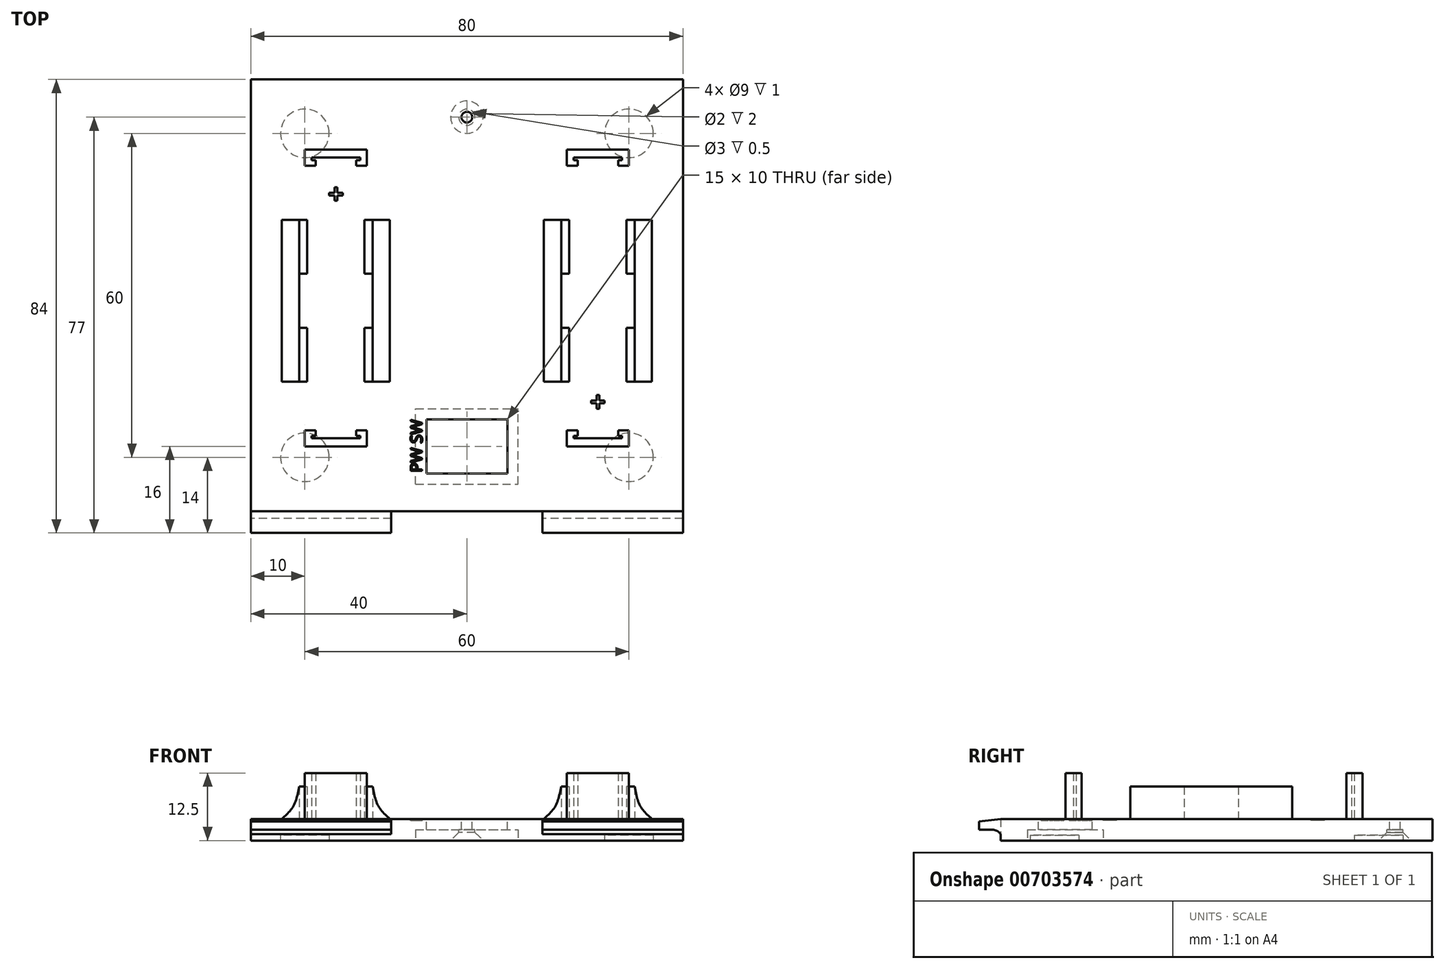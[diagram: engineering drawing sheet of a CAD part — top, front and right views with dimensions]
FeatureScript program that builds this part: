
annotation { "Feature Type Name" : "Feature", "Feature Type Description" : "" }
export const myFeature = defineFeature(function(context is Context, id is Id, definition is map)
    precondition{}
    {
        {
            var Q0;
            Q0=qCreatedBy(makeId("Top.planeOp"),FACE);
            var sketch = newSketch(context, id + "F0", { "sketchPlane" : qUnion([Q0])});
            skLineSegment(sketch, "E0.bottom", {"start": v(-40, 40) * mm, "end": v(40, 40) * mm});
            skLineSegment(sketch, "E0.top", {"start": v(-40, -40) * mm, "end": v(40, -40) * mm});
            skLineSegment(sketch, "E0.left", {"start": v(-40, 40) * mm, "end": v(-40, -40) * mm});
            skLineSegment(sketch, "E0.right", {"start": v(40, 40) * mm, "end": v(40, -40) * mm});
            skLineSegment(sketch, "E1.bottom", {"start": v(-40, -40) * mm, "end": v(-20, -40) * mm});
            skLineSegment(sketch, "E1.top", {"start": v(-40, -44) * mm, "end": v(-20, -44) * mm});
            skLineSegment(sketch, "E1.left", {"start": v(-40, -40) * mm, "end": v(-40, -44) * mm});
            skLineSegment(sketch, "E1.right", {"start": v(-20, -40) * mm, "end": v(-20, -44) * mm});
            skLineSegment(sketch, "E2.bottom", {"start": v(20, -40) * mm, "end": v(40, -40) * mm});
            skLineSegment(sketch, "E2.top", {"start": v(20, -44) * mm, "end": v(40, -44) * mm});
            skLineSegment(sketch, "E2.left", {"start": v(20, -40) * mm, "end": v(20, -44) * mm});
            skLineSegment(sketch, "E2.right", {"start": v(40, -40) * mm, "end": v(40, -44) * mm});
            skLineSegment(sketch, "E3", {"start": v(-20, -44) * mm, "end": v(20, -44) * mm});
            skLineSegment(sketch, "E4", {"start": v(-20, -40) * mm, "end": v(20, -40) * mm});
            skLineSegment(sketch, "E5", {"start": v(-14, -44) * mm, "end": v(-14, -40) * mm});
            skLineSegment(sketch, "E6", {"start": v(14, -44) * mm, "end": v(14, -40) * mm});
            skPoint(sketch, "E6.endSnap0", {"position": v(0, -40) * mm});
            skSolve(sketch);
        }
        {
            var Q0;
            Q0=makeQuery(id+"F0.imprint","IMPRINT",FACE,{"disambiguationData":[TD([[makeQuery(id+"F0.imprint","IMPRINT",EDGE,{"derivedFrom":sQuery(id+"F0.wireOp",EDGE,"E0.bottom")}),-1.0]])]});
            extrude(context, id + "F1", {"entities" : qUnion([Q0]), "depth" : 4 * mm, "offsetDistance" : 25 * mm});
        }
        {
            var Q0;
            Q0=makeQuery(id+"F1.opExtrude","CAP_FACE",FACE,{"disambiguationData":[OSD([sQuery(id+"F0.wireOp",EDGE,"E0.bottom"),sQuery(id+"F0.wireOp",EDGE,"E0.top"),sQuery(id+"F0.wireOp",EDGE,"E0.left"),sQuery(id+"F0.wireOp",EDGE,"E0.right")])],"isStart":false});
            var sketch = newSketch(context, id + "F2", { "sketchPlane" : qUnion([Q0])});
            skLineSegment(sketch, "E7.bottom", {"start": v(-30, 27) * mm, "end": v(-28, 27) * mm});
            skLineSegment(sketch, "E7.top", {"start": v(-30, 24) * mm, "end": v(-28, 24) * mm});
            skLineSegment(sketch, "E7.left", {"start": v(-30, 27) * mm, "end": v(-30, 24) * mm});
            skLineSegment(sketch, "E7.right", {"start": v(-28, 27) * mm, "end": v(-28, 24) * mm});
            skLineSegment(sketch, "E8.bottom", {"start": v(-20.5, 27) * mm, "end": v(-18.5, 27) * mm});
            skLineSegment(sketch, "E8.top", {"start": v(-20.5, 24) * mm, "end": v(-18.5, 24) * mm});
            skLineSegment(sketch, "E8.left", {"start": v(-20.5, 27) * mm, "end": v(-20.5, 24) * mm});
            skLineSegment(sketch, "E8.right", {"start": v(-18.5, 27) * mm, "end": v(-18.5, 24) * mm});
            skLineSegment(sketch, "E9", {"start": v(-28, 27) * mm, "end": v(-20.5, 27) * mm});
            skLineSegment(sketch, "E10", {"start": v(-28, 25) * mm, "end": v(-20.5, 25) * mm, "construction": true});
            skLineSegment(sketch, "E11", {"start": v(-28, 25.5) * mm, "end": v(-20.5, 25.5) * mm});
            skLineSegment(sketch, "E12", {"start": v(-28, 25.5) * mm, "end": v(-28.75, 25.5) * mm});
            skLineSegment(sketch, "E13", {"start": v(-28.75, 25.5) * mm, "end": v(-28.75, 25) * mm});
            skLineSegment(sketch, "E14", {"start": v(-28.75, 25) * mm, "end": v(-28, 25) * mm});
            skLineSegment(sketch, "E15", {"start": v(-20.5, 25.5) * mm, "end": v(-19.75, 25.5) * mm});
            skLineSegment(sketch, "E16", {"start": v(-19.75, 25.5) * mm, "end": v(-19.75, 25) * mm});
            skLineSegment(sketch, "E17", {"start": v(-19.75, 25) * mm, "end": v(-20.5, 25) * mm});
            skLineSegment(sketch, "E18.bottom", {"start": v(-18.5, -28) * mm, "end": v(-20.5, -28) * mm});
            skLineSegment(sketch, "E18.top", {"start": v(-18.5, -25) * mm, "end": v(-20.5, -25) * mm});
            skLineSegment(sketch, "E18.left", {"start": v(-18.5, -28) * mm, "end": v(-18.5, -25) * mm});
            skLineSegment(sketch, "E18.right", {"start": v(-20.5, -28) * mm, "end": v(-20.5, -25) * mm});
            skLineSegment(sketch, "E19.bottom", {"start": v(-28, -28) * mm, "end": v(-30, -28) * mm});
            skLineSegment(sketch, "E19.top", {"start": v(-28, -25) * mm, "end": v(-30, -25) * mm});
            skLineSegment(sketch, "E19.left", {"start": v(-28, -28) * mm, "end": v(-28, -25) * mm});
            skLineSegment(sketch, "E19.right", {"start": v(-30, -28) * mm, "end": v(-30, -25) * mm});
            skLineSegment(sketch, "E20", {"start": v(-20.5, -28) * mm, "end": v(-28, -28) * mm});
            skLineSegment(sketch, "E21", {"start": v(-20.5, -26) * mm, "end": v(-28, -26) * mm, "construction": true});
            skLineSegment(sketch, "E22", {"start": v(-20.5, -26.5) * mm, "end": v(-28, -26.5) * mm});
            skLineSegment(sketch, "E23", {"start": v(-20.5, -26.5) * mm, "end": v(-19.75, -26.5) * mm});
            skLineSegment(sketch, "E24", {"start": v(-19.75, -26.5) * mm, "end": v(-19.75, -26) * mm});
            skLineSegment(sketch, "E25", {"start": v(-19.75, -26) * mm, "end": v(-20.5, -26) * mm});
            skLineSegment(sketch, "E26", {"start": v(-28, -26.5) * mm, "end": v(-28.75, -26.5) * mm});
            skLineSegment(sketch, "E27", {"start": v(-28.75, -26.5) * mm, "end": v(-28.75, -26) * mm});
            skLineSegment(sketch, "E28", {"start": v(-28.75, -26) * mm, "end": v(-28, -26) * mm});
            skLineSegment(sketch, "E29.bottom", {"start": v(18.5, 27) * mm, "end": v(20.5, 27) * mm});
            skLineSegment(sketch, "E29.top", {"start": v(18.5, 24) * mm, "end": v(20.5, 24) * mm});
            skLineSegment(sketch, "E29.left", {"start": v(18.5, 27) * mm, "end": v(18.5, 24) * mm});
            skLineSegment(sketch, "E29.right", {"start": v(20.5, 27) * mm, "end": v(20.5, 24) * mm});
            skLineSegment(sketch, "E30.bottom", {"start": v(28, 27) * mm, "end": v(30, 27) * mm});
            skLineSegment(sketch, "E30.top", {"start": v(28, 24) * mm, "end": v(30, 24) * mm});
            skLineSegment(sketch, "E30.left", {"start": v(28, 27) * mm, "end": v(28, 24) * mm});
            skLineSegment(sketch, "E30.right", {"start": v(30, 27) * mm, "end": v(30, 24) * mm});
            skLineSegment(sketch, "E31", {"start": v(20.5, 27) * mm, "end": v(28, 27) * mm});
            skLineSegment(sketch, "E32", {"start": v(20.5, 25) * mm, "end": v(28, 25) * mm, "construction": true});
            skLineSegment(sketch, "E33", {"start": v(20.5, 25.5) * mm, "end": v(28, 25.5) * mm});
            skLineSegment(sketch, "E34", {"start": v(20.5, 25.5) * mm, "end": v(19.75, 25.5) * mm});
            skLineSegment(sketch, "E35", {"start": v(19.75, 25.5) * mm, "end": v(19.75, 25) * mm});
            skLineSegment(sketch, "E36", {"start": v(19.75, 25) * mm, "end": v(20.5, 25) * mm});
            skLineSegment(sketch, "E37", {"start": v(28, 25.5) * mm, "end": v(28.75, 25.5) * mm});
            skLineSegment(sketch, "E38", {"start": v(28.75, 25.5) * mm, "end": v(28.75, 25) * mm});
            skLineSegment(sketch, "E39", {"start": v(28.75, 25) * mm, "end": v(28, 25) * mm});
            skLineSegment(sketch, "E40.bottom", {"start": v(30, -28) * mm, "end": v(28, -28) * mm});
            skLineSegment(sketch, "E40.top", {"start": v(30, -25) * mm, "end": v(28, -25) * mm});
            skLineSegment(sketch, "E40.left", {"start": v(30, -28) * mm, "end": v(30, -25) * mm});
            skLineSegment(sketch, "E40.right", {"start": v(28, -28) * mm, "end": v(28, -25) * mm});
            skLineSegment(sketch, "E41.bottom", {"start": v(20.5, -28) * mm, "end": v(18.5, -28) * mm});
            skLineSegment(sketch, "E41.top", {"start": v(20.5, -25) * mm, "end": v(18.5, -25) * mm});
            skLineSegment(sketch, "E41.left", {"start": v(20.5, -28) * mm, "end": v(20.5, -25) * mm});
            skLineSegment(sketch, "E41.right", {"start": v(18.5, -28) * mm, "end": v(18.5, -25) * mm});
            skLineSegment(sketch, "E42", {"start": v(28, -28) * mm, "end": v(20.5, -28) * mm});
            skLineSegment(sketch, "E43", {"start": v(28, -26) * mm, "end": v(20.5, -26) * mm, "construction": true});
            skLineSegment(sketch, "E44", {"start": v(28, -26.5) * mm, "end": v(20.5, -26.5) * mm});
            skLineSegment(sketch, "E45", {"start": v(28, -26.5) * mm, "end": v(28.75, -26.5) * mm});
            skLineSegment(sketch, "E46", {"start": v(28.75, -26.5) * mm, "end": v(28.75, -26) * mm});
            skLineSegment(sketch, "E47", {"start": v(28.75, -26) * mm, "end": v(28, -26) * mm});
            skLineSegment(sketch, "E48", {"start": v(20.5, -26.5) * mm, "end": v(19.75, -26.5) * mm});
            skLineSegment(sketch, "E49", {"start": v(19.75, -26.5) * mm, "end": v(19.75, -26) * mm});
            skLineSegment(sketch, "E50", {"start": v(19.75, -26) * mm, "end": v(20.5, -26) * mm});
            skLineSegment(sketch, "E51", {"start": v(-18.5, 27) * mm, "end": v(18.5, 27) * mm, "construction": true});
            skLineSegment(sketch, "E52", {"start": v(-24.25, 25) * mm, "end": v(-24.25, -26) * mm, "construction": true});
            skLineSegment(sketch, "E53", {"start": v(24.25, 25) * mm, "end": v(24.25, -26) * mm, "construction": true});
            skLineSegment(sketch, "E54.bottom", {"start": v(-31.05, 14) * mm, "end": v(-29.55, 14) * mm});
            skLineSegment(sketch, "E54.top", {"start": v(-31.05, 4) * mm, "end": v(-29.55, 4) * mm});
            skLineSegment(sketch, "E54.left", {"start": v(-31.05, 14) * mm, "end": v(-31.05, 4) * mm});
            skLineSegment(sketch, "E54.right", {"start": v(-29.55, 14) * mm, "end": v(-29.55, 4) * mm});
            skLineSegment(sketch, "E55", {"start": v(-30, 24) * mm, "end": v(-42.81, 24) * mm, "construction": true});
            skLineSegment(sketch, "E56.bottom", {"start": v(-31.05, -6) * mm, "end": v(-29.55, -6) * mm});
            skLineSegment(sketch, "E56.top", {"start": v(-31.05, -16) * mm, "end": v(-29.55, -16) * mm});
            skLineSegment(sketch, "E56.left", {"start": v(-31.05, -6) * mm, "end": v(-31.05, -16) * mm});
            skLineSegment(sketch, "E56.right", {"start": v(-29.55, -6) * mm, "end": v(-29.55, -16) * mm});
            skLineSegment(sketch, "E57.MirrorCS", {"start": v(-18.95, 14) * mm, "end": v(-18.95, 4) * mm});
            skLineSegment(sketch, "E58.MirrorCS", {"start": v(-17.45, 14) * mm, "end": v(-17.45, 4) * mm});
            skLineSegment(sketch, "E59.MirrorCS", {"start": v(-17.45, 14) * mm, "end": v(-18.95, 14) * mm});
            skLineSegment(sketch, "E60.MirrorCS", {"start": v(-17.45, 4) * mm, "end": v(-18.95, 4) * mm});
            skLineSegment(sketch, "E61.MirrorCS", {"start": v(-18.95, -6) * mm, "end": v(-18.95, -16) * mm});
            skLineSegment(sketch, "E62.MirrorCS", {"start": v(-17.45, -6) * mm, "end": v(-17.45, -16) * mm});
            skLineSegment(sketch, "E63.MirrorCS", {"start": v(-17.45, -6) * mm, "end": v(-18.95, -6) * mm});
            skLineSegment(sketch, "E64.MirrorCS", {"start": v(-17.45, -16) * mm, "end": v(-18.95, -16) * mm});
            skLineSegment(sketch, "E65", {"start": v(18.5, 24) * mm, "end": v(3.37, 24) * mm, "construction": true});
            skLineSegment(sketch, "E66.bottom", {"start": v(17.45, 14) * mm, "end": v(18.95, 14) * mm});
            skLineSegment(sketch, "E66.top", {"start": v(17.45, 4) * mm, "end": v(18.95, 4) * mm});
            skLineSegment(sketch, "E66.left", {"start": v(17.45, 14) * mm, "end": v(17.45, 4) * mm});
            skLineSegment(sketch, "E66.right", {"start": v(18.95, 14) * mm, "end": v(18.95, 4) * mm});
            skLineSegment(sketch, "E67.bottom", {"start": v(17.45, -6) * mm, "end": v(18.95, -6) * mm});
            skLineSegment(sketch, "E67.top", {"start": v(17.45, -16) * mm, "end": v(18.95, -16) * mm});
            skLineSegment(sketch, "E67.left", {"start": v(17.45, -6) * mm, "end": v(17.45, -16) * mm});
            skLineSegment(sketch, "E67.right", {"start": v(18.95, -6) * mm, "end": v(18.95, -16) * mm});
            skLineSegment(sketch, "E68.MirrorCS", {"start": v(29.55, 14) * mm, "end": v(29.55, 4) * mm});
            skLineSegment(sketch, "E69.MirrorCS", {"start": v(31.05, 14) * mm, "end": v(31.05, 4) * mm});
            skLineSegment(sketch, "E70.MirrorCS", {"start": v(31.05, 4) * mm, "end": v(29.55, 4) * mm});
            skLineSegment(sketch, "E71.MirrorCS", {"start": v(31.05, 14) * mm, "end": v(29.55, 14) * mm});
            skLineSegment(sketch, "E72.MirrorCS", {"start": v(31.05, -6) * mm, "end": v(29.55, -6) * mm});
            skLineSegment(sketch, "E73.MirrorCS", {"start": v(29.55, -6) * mm, "end": v(29.55, -16) * mm});
            skLineSegment(sketch, "E74.MirrorCS", {"start": v(31.05, -6) * mm, "end": v(31.05, -16) * mm});
            skLineSegment(sketch, "E75.MirrorCS", {"start": v(31.05, -16) * mm, "end": v(29.55, -16) * mm});
            skLineSegment(sketch, "E76", {"start": v(-28, -25) * mm, "end": v(-20.5, -25) * mm, "construction": true});
            skLineSegment(sketch, "E77", {"start": v(20.5, -25) * mm, "end": v(28, -25) * mm, "construction": true});
            skLineSegment(sketch, "E78", {"start": v(20.5, 24) * mm, "end": v(28, 24) * mm, "construction": true});
            skLineSegment(sketch, "E79", {"start": v(-28, 24) * mm, "end": v(-20.5, 24) * mm, "construction": true});
            skLineSegment(sketch, "E80.bottom", {"start": v(-24.5, 20) * mm, "end": v(-24, 20) * mm});
            skLineSegment(sketch, "E80.top", {"start": v(-24.5, 17.5) * mm, "end": v(-24, 17.5) * mm});
            skLineSegment(sketch, "E80.left", {"start": v(-24.5, 20) * mm, "end": v(-24.5, 19) * mm});
            skLineSegment(sketch, "E80.right", {"start": v(-24, 20) * mm, "end": v(-24, 19) * mm});
            skLineSegment(sketch, "E81.bottom", {"start": v(-23, 19) * mm, "end": v(-24, 19) * mm});
            skLineSegment(sketch, "E81.top", {"start": v(-23, 18.5) * mm, "end": v(-24, 18.5) * mm});
            skLineSegment(sketch, "E81.left", {"start": v(-23, 19) * mm, "end": v(-23, 18.5) * mm});
            skLineSegment(sketch, "E81.right", {"start": v(-25.5, 19) * mm, "end": v(-25.5, 18.5) * mm});
            skLineSegment(sketch, "E82", {"start": v(-25.5, 18.75) * mm, "end": v(-23, 18.75) * mm, "construction": true});
            skLineSegment(sketch, "E83", {"start": v(-24.25, 20) * mm, "end": v(-24.25, 17.5) * mm, "construction": true});
            skLineSegment(sketch, "E84.trimOffspring", {"start": v(-24.5, 18.5) * mm, "end": v(-24.5, 17.5) * mm});
            skLineSegment(sketch, "E85.trimOffspring", {"start": v(-24.5, 18.5) * mm, "end": v(-25.5, 18.5) * mm});
            skLineSegment(sketch, "E86.trimOffspring", {"start": v(-24, 18.5) * mm, "end": v(-24, 17.5) * mm});
            skLineSegment(sketch, "E87.trimOffspring", {"start": v(-24.5, 19) * mm, "end": v(-25.5, 19) * mm});
            skLineSegment(sketch, "E88.bottom", {"start": v(24, -18.5) * mm, "end": v(24.5, -18.5) * mm});
            skLineSegment(sketch, "E88.top", {"start": v(24, -21) * mm, "end": v(24.5, -21) * mm});
            skLineSegment(sketch, "E88.left", {"start": v(24, -18.5) * mm, "end": v(24, -19.5) * mm});
            skLineSegment(sketch, "E88.right", {"start": v(24.5, -18.5) * mm, "end": v(24.5, -19.5) * mm});
            skLineSegment(sketch, "E89.bottom", {"start": v(25.5, -19.5) * mm, "end": v(24.5, -19.5) * mm});
            skLineSegment(sketch, "E89.top", {"start": v(25.5, -20) * mm, "end": v(24.5, -20) * mm});
            skLineSegment(sketch, "E89.left", {"start": v(25.5, -19.5) * mm, "end": v(25.5, -20) * mm});
            skLineSegment(sketch, "E89.right", {"start": v(23, -19.5) * mm, "end": v(23, -20) * mm});
            skLineSegment(sketch, "E90", {"start": v(23, -19.75) * mm, "end": v(25.5, -19.75) * mm, "construction": true});
            skLineSegment(sketch, "E91", {"start": v(24.25, -18.5) * mm, "end": v(24.25, -21) * mm, "construction": true});
            skLineSegment(sketch, "E92.trimOffspring", {"start": v(24, -20) * mm, "end": v(24, -21) * mm});
            skLineSegment(sketch, "E93.trimOffspring", {"start": v(24, -20) * mm, "end": v(23, -20) * mm});
            skLineSegment(sketch, "E94.trimOffspring", {"start": v(24.5, -20) * mm, "end": v(24.5, -21) * mm});
            skLineSegment(sketch, "E95.trimOffspring", {"start": v(24, -19.5) * mm, "end": v(23, -19.5) * mm});
            skSolve(sketch);
        }
        {
            var Q0;
            Q0=makeQuery(id+"F2.imprint","IMPRINT",FACE,{"disambiguationData":[TD([[makeQuery(id+"F2.imprint","IMPRINT",EDGE,{"derivedFrom":sQuery(id+"F2.wireOp",EDGE,"E56.bottom")}),-1.0]])]});
            var Q1;
            Q1=makeQuery(id+"F2.imprint","IMPRINT",FACE,{"disambiguationData":[TD([[makeQuery(id+"F2.imprint","IMPRINT",EDGE,{"derivedFrom":sQuery(id+"F2.wireOp",EDGE,"E61.MirrorCS")}),1.0]])]});
            var Q2;
            Q2=makeQuery(id+"F2.imprint","IMPRINT",FACE,{"disambiguationData":[TD([[makeQuery(id+"F2.imprint","IMPRINT",EDGE,{"derivedFrom":sQuery(id+"F2.wireOp",EDGE,"E57.MirrorCS")}),1.0]])]});
            var Q3;
            Q3=makeQuery(id+"F2.imprint","IMPRINT",FACE,{"disambiguationData":[TD([[makeQuery(id+"F2.imprint","IMPRINT",EDGE,{"derivedFrom":sQuery(id+"F2.wireOp",EDGE,"E54.bottom")}),-1.0]])]});
            var Q4;
            Q4=makeQuery(id+"F2.imprint","IMPRINT",FACE,{"disambiguationData":[TD([[makeQuery(id+"F2.imprint","IMPRINT",EDGE,{"derivedFrom":sQuery(id+"F2.wireOp",EDGE,"E67.bottom")}),-1.0]])]});
            var Q5;
            Q5=makeQuery(id+"F2.imprint","IMPRINT",FACE,{"disambiguationData":[TD([[makeQuery(id+"F2.imprint","IMPRINT",EDGE,{"derivedFrom":sQuery(id+"F2.wireOp",EDGE,"E66.bottom")}),-1.0]])]});
            var Q6;
            Q6=makeQuery(id+"F2.imprint","IMPRINT",FACE,{"disambiguationData":[TD([[makeQuery(id+"F2.imprint","IMPRINT",EDGE,{"derivedFrom":sQuery(id+"F2.wireOp",EDGE,"E68.MirrorCS")}),1.0]])]});
            var Q7;
            Q7=makeQuery(id+"F2.imprint","IMPRINT",FACE,{"disambiguationData":[TD([[makeQuery(id+"F2.imprint","IMPRINT",EDGE,{"derivedFrom":sQuery(id+"F2.wireOp",EDGE,"E72.MirrorCS")}),1.0]])]});
            extrude(context, id + "F3", {"entities" : qUnion([Q0, Q1, Q2, Q3, Q4, Q5, Q6, Q7]), "operationType" : NewBodyOperationType.ADD, "depth" : 6 * mm, "offsetDistance" : 25 * mm});
        }
        {
            var Q0;
            {var subQ1=sQuery(id+"F2.wireOp",EDGE,"E7.bottom");Q0=makeQuery(id+"F2.imprint","IMPRINT",FACE,{"disambiguationData":[TD([[makeQuery(id+"F2.imprint","IMPRINT",EDGE,{"derivedFrom":subQ1}),-1.0]])]});}
            var Q1;
            {var subQ0=sQuery(id+"F2.wireOp",EDGE,"E9");Q1=makeQuery(id+"F2.imprint","IMPRINT",FACE,{"disambiguationData":[TD([[makeQuery(id+"F2.imprint","IMPRINT",EDGE,{"derivedFrom":subQ0}),-1.0]])]});}
            var Q2;
            {var subQ3=sQuery(id+"F2.wireOp",EDGE,"E8.bottom");Q2=makeQuery(id+"F2.imprint","IMPRINT",FACE,{"disambiguationData":[TD([[makeQuery(id+"F2.imprint","IMPRINT",EDGE,{"derivedFrom":subQ3}),-1.0]])]});}
            var Q3;
            {var subQ1=sQuery(id+"F2.wireOp",EDGE,"E18.bottom");Q3=makeQuery(id+"F2.imprint","IMPRINT",FACE,{"disambiguationData":[TD([[makeQuery(id+"F2.imprint","IMPRINT",EDGE,{"derivedFrom":subQ1}),-1.0]])]});}
            var Q4;
            {var subQ0=sQuery(id+"F2.wireOp",EDGE,"E20");Q4=makeQuery(id+"F2.imprint","IMPRINT",FACE,{"disambiguationData":[TD([[makeQuery(id+"F2.imprint","IMPRINT",EDGE,{"derivedFrom":subQ0}),-1.0]])]});}
            var Q5;
            {var subQ3=sQuery(id+"F2.wireOp",EDGE,"E19.bottom");Q5=makeQuery(id+"F2.imprint","IMPRINT",FACE,{"disambiguationData":[TD([[makeQuery(id+"F2.imprint","IMPRINT",EDGE,{"derivedFrom":subQ3}),-1.0]])]});}
            var Q6;
            {var subQ1=sQuery(id+"F2.wireOp",EDGE,"E29.bottom");Q6=makeQuery(id+"F2.imprint","IMPRINT",FACE,{"disambiguationData":[TD([[makeQuery(id+"F2.imprint","IMPRINT",EDGE,{"derivedFrom":subQ1}),-1.0]])]});}
            var Q7;
            {var subQ0=sQuery(id+"F2.wireOp",EDGE,"E31");Q7=makeQuery(id+"F2.imprint","IMPRINT",FACE,{"disambiguationData":[TD([[makeQuery(id+"F2.imprint","IMPRINT",EDGE,{"derivedFrom":subQ0}),-1.0]])]});}
            var Q8;
            {var subQ3=sQuery(id+"F2.wireOp",EDGE,"E30.bottom");Q8=makeQuery(id+"F2.imprint","IMPRINT",FACE,{"disambiguationData":[TD([[makeQuery(id+"F2.imprint","IMPRINT",EDGE,{"derivedFrom":subQ3}),-1.0]])]});}
            var Q9;
            {var subQ1=sQuery(id+"F2.wireOp",EDGE,"E40.bottom");Q9=makeQuery(id+"F2.imprint","IMPRINT",FACE,{"disambiguationData":[TD([[makeQuery(id+"F2.imprint","IMPRINT",EDGE,{"derivedFrom":subQ1}),-1.0]])]});}
            var Q10;
            {var subQ0=sQuery(id+"F2.wireOp",EDGE,"E42");Q10=makeQuery(id+"F2.imprint","IMPRINT",FACE,{"disambiguationData":[TD([[makeQuery(id+"F2.imprint","IMPRINT",EDGE,{"derivedFrom":subQ0}),-1.0]])]});}
            var Q11;
            {var subQ3=sQuery(id+"F2.wireOp",EDGE,"E41.bottom");Q11=makeQuery(id+"F2.imprint","IMPRINT",FACE,{"disambiguationData":[TD([[makeQuery(id+"F2.imprint","IMPRINT",EDGE,{"derivedFrom":subQ3}),-1.0]])]});}
            extrude(context, id + "F4", {"entities" : qUnion([Q0, Q1, Q2, Q3, Q4, Q5, Q6, Q7, Q8, Q9, Q10, Q11]), "operationType" : NewBodyOperationType.ADD, "depth" : 8.5 * mm, "offsetDistance" : 25 * mm});
        }
        {
            var Q0;
            Q0=qCreatedBy(makeId("Front.planeOp"),FACE);
            var sketch = newSketch(context, id + "F5", { "sketchPlane" : qUnion([Q0])});
            skLineSegment(sketch, "E96.top", {"start": v(-34.24, 4) * mm, "end": v(-31.05, 4) * mm});
            skLineSegment(sketch, "E96.right", {"start": v(-31.05, 10) * mm, "end": v(-31.05, 4) * mm});
            skPoint(sketch, "E97", {"position": v(-34.24, 4) * mm});
            skFitSpline(sketch, "E98", {"points": [v(-31.05, 10) * mm, v(-32.1, 6.43) * mm, v(-34.24, 4) * mm], "startDerivative": vector(-1.38, -7.39) * mm, "endDerivative": vector(-5.04, -4.58) * mm});
            skLineSegment(sketch, "E99", {"start": v(-24.25, 13.7) * mm, "end": v(-24.25, 3.33) * mm, "construction": true});
            skFitSpline(sketch, "E100.MirrorCS", {"points": [v(-17.45, 10) * mm, v(-16.4, 6.43) * mm, v(-14.26, 4) * mm], "startDerivative": vector(1.38, -7.39) * mm, "endDerivative": vector(5.04, -4.58) * mm});
            skLineSegment(sketch, "E101", {"start": v(24.25, 13.97) * mm, "end": v(24.25, 2.5) * mm, "construction": true});
            skLineSegment(sketch, "E102.MirrorCS", {"start": v(-17.45, 10) * mm, "end": v(-17.45, 4) * mm});
            skLineSegment(sketch, "E103.MirrorCS", {"start": v(-14.26, 4) * mm, "end": v(-17.45, 4) * mm});
            skFitSpline(sketch, "E104.MirrorCS", {"points": [v(17.45, 10) * mm, v(16.4, 6.43) * mm, v(14.26, 4) * mm], "startDerivative": vector(-1.38, -7.39) * mm, "endDerivative": vector(-5.04, -4.58) * mm});
            skFitSpline(sketch, "E105.MirrorCS", {"points": [v(31.05, 10) * mm, v(32.1, 6.43) * mm, v(34.24, 4) * mm], "startDerivative": vector(1.38, -7.39) * mm, "endDerivative": vector(5.04, -4.58) * mm});
            skLineSegment(sketch, "E106.MirrorCS", {"start": v(34.24, 4) * mm, "end": v(31.05, 4) * mm});
            skLineSegment(sketch, "E107.MirrorCS", {"start": v(31.05, 10) * mm, "end": v(31.05, 4) * mm});
            skLineSegment(sketch, "E108.MirrorCS", {"start": v(17.45, 10) * mm, "end": v(17.45, 4) * mm});
            skLineSegment(sketch, "E109.MirrorCS", {"start": v(14.26, 4) * mm, "end": v(17.45, 4) * mm});
            skSolve(sketch);
        }
        {
            var Q0;
            Q0=makeQuery(id+"F1.opExtrude","CAP_FACE",FACE,{"disambiguationData":[OSD([sQuery(id+"F0.wireOp",EDGE,"E0.bottom"),sQuery(id+"F0.wireOp",EDGE,"E0.top"),sQuery(id+"F0.wireOp",EDGE,"E0.left"),sQuery(id+"F0.wireOp",EDGE,"E0.right")])],"isStart":false});
            var sketch = newSketch(context, id + "F6", { "sketchPlane" : qUnion([Q0])});
            skCircle(sketch, "E110", {"center": v(0, 33) * mm, "radius": 1.5 * mm});
            skCircle(sketch, "E111", {"center": v(0, 33) * mm, "radius": 1 * mm});
            skSolve(sketch);
        }
        {
            var Q0;
            Q0=makeQuery(id+"F6.imprint","IMPRINT",FACE,{"disambiguationData":[TD([[makeQuery(id+"F6.imprint","IMPRINT",EDGE,{"derivedFrom":sQuery(id+"F6.wireOp",EDGE,"E111")}),1.0]])]});
            extrude(context, id + "F7", {"entities" : qUnion([Q0]), "operationType" : NewBodyOperationType.REMOVE, "oppositeDirection" : true, "depth" : 25 * mm, "offsetDistance" : 25 * mm});
        }
        {
            var Q0;
            Q0=makeQuery(id+"F6.imprint","IMPRINT",FACE,{"disambiguationData":[TD([[makeQuery(id+"F6.imprint","IMPRINT",EDGE,{"derivedFrom":sQuery(id+"F6.wireOp",EDGE,"E110")}),1.0]])]});
            extrude(context, id + "F8", {"entities" : qUnion([Q0]), "operationType" : NewBodyOperationType.REMOVE, "oppositeDirection" : true, "depth" : 25 * mm, "offsetDistance" : 25 * mm, "hasSecondDirection" : true, "secondDirectionOppositeDirection" : true, "secondDirectionDepth" : 2 * mm});
        }
        {
            var Q0;
            Q0=makeQuery(id+"F8.boolean.opBoolean","INTERSECT",EDGE,{"derivedFrom":[makeQuery(id+"F1.opExtrude","CAP_FACE",FACE,{"disambiguationData":[OSD([sQuery(id+"F0.wireOp",EDGE,"E0.bottom"),sQuery(id+"F0.wireOp",EDGE,"E0.top"),sQuery(id+"F0.wireOp",EDGE,"E0.left"),sQuery(id+"F0.wireOp",EDGE,"E0.right")])],"isStart":true}),makeQuery(id+"F8.opExtrude","SWEPT_FACE",FACE,{"disambiguationData":[OSD([sQuery(id+"F6.wireOp",EDGE,"E110")])]})]});
            chamfer(context, id + "F9", {"entities" : qUnion([Q0]), "width" : 1.5 * mm, "tangentPropagation" : true});
        }
        {
            var Q0;
            Q0=qCreatedBy(makeId("Right.planeOp"),FACE);
            var sketch = newSketch(context, id + "F10", { "sketchPlane" : qUnion([Q0])});
            skLineSegment(sketch, "E112", {"start": v(-44, 2) * mm, "end": v(-40, 2) * mm});
            skLineSegment(sketch, "E113", {"start": v(-44, 4) * mm, "end": v(-40, 4) * mm});
            skLineSegment(sketch, "E114", {"start": v(-44, 4) * mm, "end": v(-44, 2) * mm});
            skLineSegment(sketch, "E115", {"start": v(-40, 2) * mm, "end": v(-40, 4) * mm});
            skLineSegment(sketch, "E116", {"start": v(-47.4, 0) * mm, "end": v(-39.16, 0) * mm});
            skLineSegment(sketch, "E117", {"start": v(-40, 2) * mm, "end": v(-40, 0) * mm});
            skFitSpline(sketch, "E118", {"points": [v(-40, 1.17) * mm, v(-40.47, 1.69) * mm, v(-41.33, 2) * mm], "startDerivative": vector(-0.67, 1.12) * mm, "endDerivative": vector(-1.92, 0.56) * mm});
            skLineSegment(sketch, "E119", {"start": v(-44, 3.5) * mm, "end": v(-40, 4) * mm});
            skSolve(sketch);
        }
        {
            var Q0;
            {var subQ4=sQuery(id+"F10.wireOp",EDGE,"E115");Q0=makeQuery(id+"F10.imprint","IMPRINT",FACE,{"disambiguationData":[TD([[makeQuery(id+"F10.imprint","IMPRINT",EDGE,{"derivedFrom":subQ4}),1.0]])]});}
            var Q1;
            {var subQ3=sQuery(id+"F10.wireOp",EDGE,"E118");Q1=makeQuery(id+"F10.imprint","IMPRINT",FACE,{"disambiguationData":[TD([[makeQuery(id+"F10.imprint","IMPRINT",EDGE,{"derivedFrom":subQ3}),-1.0]])]});}
            extrude(context, id + "F11", {"entities" : qUnion([Q0, Q1]), "operationType" : NewBodyOperationType.ADD, "depth" : 40 * mm, "offsetDistance" : 25 * mm, "hasSecondDirection" : true, "secondDirectionOppositeDirection" : true, "secondDirectionDepth" : 40 * mm});
        }
        {
            var Q0;
            Q0=makeQuery(id+"F0.imprint","IMPRINT",FACE,{"disambiguationData":[TD([[makeQuery(id+"F0.imprint","IMPRINT",EDGE,{"derivedFrom":sQuery(id+"F0.wireOp",EDGE,"E1.bottom")}),-1.0]])]});
            var Q1;
            {var subQ0=sQuery(id+"F0.wireOp",EDGE,"E5");Q1=makeQuery(id+"F0.imprint","IMPRINT",FACE,{"disambiguationData":[TD([[makeQuery(id+"F0.imprint","IMPRINT",EDGE,{"derivedFrom":subQ0}),-1.0]])]});}
            var Q2;
            Q2=makeQuery(id+"F0.imprint","IMPRINT",FACE,{"disambiguationData":[TD([[makeQuery(id+"F0.imprint","IMPRINT",EDGE,{"derivedFrom":sQuery(id+"F0.wireOp",EDGE,"E2.bottom")}),-1.0]])]});
            extrude(context, id + "F12", {"entities" : qUnion([Q0, Q1, Q2]), "operationType" : NewBodyOperationType.REMOVE, "depth" : 18.6 * mm, "offsetDistance" : 25 * mm});
        }
        {
            var Q0;
            Q0=makeQuery(id+"F2.imprint","IMPRINT",FACE,{"disambiguationData":[TD([[makeQuery(id+"F2.imprint","IMPRINT",EDGE,{"derivedFrom":sQuery(id+"F2.wireOp",EDGE,"E80.bottom")}),-1.0]])]});
            var Q1;
            Q1=makeQuery(id+"F2.imprint","IMPRINT",FACE,{"disambiguationData":[TD([[makeQuery(id+"F2.imprint","IMPRINT",EDGE,{"derivedFrom":sQuery(id+"F2.wireOp",EDGE,"E88.bottom")}),-1.0]])]});
            extrude(context, id + "F13", {"entities" : qUnion([Q0, Q1]), "operationType" : NewBodyOperationType.REMOVE, "oppositeDirection" : true, "depth" : .3 * mm, "offsetDistance" : 25 * mm});
        }
        {
            var Q0;
            Q0=makeQuery(id+"F6.imprint","IMPRINT",FACE,{"disambiguationData":[TD([[makeQuery(id+"F6.imprint","IMPRINT",EDGE,{"derivedFrom":sQuery(id+"F6.wireOp",EDGE,"E110")}),-1.0]])]});
            var sketch = newSketch(context, id + "F14", { "sketchPlane" : qUnion([Q0])});
            skLineSegment(sketch, "E120.bottom", {"start": v(-7.5, -23) * mm, "end": v(7.5, -23) * mm});
            skLineSegment(sketch, "E120.top", {"start": v(-7.5, -33) * mm, "end": v(7.5, -33) * mm});
            skLineSegment(sketch, "E120.left", {"start": v(-7.5, -23) * mm, "end": v(-7.5, -33) * mm});
            skLineSegment(sketch, "E120.right", {"start": v(7.5, -23) * mm, "end": v(7.5, -33) * mm});
            skPoint(sketch, "E121", {"position": v(0, -23) * mm});
            skText(sketch, "E122", { "text": "PW SW", "fontName": "AllertaStencil-Regular.ttf"});
            const initialGuessF14  = {"E122": [-0.00882, -0.02208, 1, 0, 0.00373]};
            skSetInitialGuess(sketch, initialGuessF14);
            skSolve(sketch);
        }
        {
            var Q0;
            Q0=makeQuery(id+"F14.imprint","IMPRINT",FACE,{"disambiguationData":[TD([[makeQuery(id+"F14.imprint","IMPRINT",EDGE,{"derivedFrom":sQuery(id+"F14.wireOp",EDGE,"E120.bottom")}),-1.0]])]});
            extrude(context, id + "F15", {"entities" : qUnion([Q0]), "operationType" : NewBodyOperationType.REMOVE, "oppositeDirection" : true, "depth" : 25 * mm, "offsetDistance" : 25 * mm});
        }
        {
            var Q0;
            Q0=makeQuery(id+"F6.imprint","IMPRINT",FACE,{"disambiguationData":[TD([[makeQuery(id+"F6.imprint","IMPRINT",EDGE,{"derivedFrom":sQuery(id+"F6.wireOp",EDGE,"E110")}),-1.0]])]});
            var sketch = newSketch(context, id + "F16", { "sketchPlane" : qUnion([Q0])});
            skText(sketch, "E123", { "text": "PW SW\n", "fontName": "OpenSans-Regular.ttf"});
            const initialGuessF16  = {"E123": [-0.00828, -0.0328, 0, 1, 0.00216]};
            skSetInitialGuess(sketch, initialGuessF16);
            skSolve(sketch);
        }
        {
            var Q0;
            Q0 = qSketchRegion(id + "F16", true);
            var Q1;
            Q1 = qConstructionFilter(qBodyType(qCreatedBy(id + "F16" ,EDGE), BodyType.WIRE), ConstructionObject.NO);
            extrude(context, id + "F17", {"entities" : qUnion([Q0]), "operationType" : NewBodyOperationType.REMOVE, "surfaceOperationType" : NewSurfaceOperationType.ADD, "surfaceEntities" : qUnion([Q1]), "oppositeDirection" : true, "depth" : .3 * mm, "offsetDistance" : 25 * mm});
        }
        {
            var Q0;
            Q0=makeQuery(id+"F0.imprint","IMPRINT",FACE,{"disambiguationData":[TD([[makeQuery(id+"F0.imprint","IMPRINT",EDGE,{"derivedFrom":sQuery(id+"F0.wireOp",EDGE,"E0.bottom")}),-1.0]])]});
            var sketch = newSketch(context, id + "F18", { "sketchPlane" : qUnion([Q0])});
            skCircle(sketch, "E124", {"center": v(-30, -30) * mm, "radius": 7 * mm});
            skCircle(sketch, "E125", {"center": v(30, -30) * mm, "radius": 7 * mm});
            skCircle(sketch, "E126", {"center": v(-30, 30) * mm, "radius": 7 * mm});
            skCircle(sketch, "E127", {"center": v(30, 30) * mm, "radius": 7 * mm});
            skCircle(sketch, "E128", {"center": v(-30, -30) * mm, "radius": 4.5 * mm});
            skCircle(sketch, "E129", {"center": v(30, -30) * mm, "radius": 4.5 * mm});
            skCircle(sketch, "E130", {"center": v(-30, 30) * mm, "radius": 4.5 * mm});
            skCircle(sketch, "E131", {"center": v(30, 30) * mm, "radius": 4.5 * mm});
            skSolve(sketch);
        }
        {
            var Q0;
            Q0=makeQuery(id+"F18.imprint","IMPRINT",FACE,{"disambiguationData":[TD([[makeQuery(id+"F18.imprint","IMPRINT",EDGE,{"derivedFrom":sQuery(id+"F18.wireOp",EDGE,"E131")}),1.0]])]});
            var Q1;
            Q1=makeQuery(id+"F18.imprint","IMPRINT",FACE,{"disambiguationData":[TD([[makeQuery(id+"F18.imprint","IMPRINT",EDGE,{"derivedFrom":sQuery(id+"F18.wireOp",EDGE,"E130")}),1.0]])]});
            var Q2;
            Q2=makeQuery(id+"F18.imprint","IMPRINT",FACE,{"disambiguationData":[TD([[makeQuery(id+"F18.imprint","IMPRINT",EDGE,{"derivedFrom":sQuery(id+"F18.wireOp",EDGE,"E128")}),1.0]])]});
            var Q3;
            Q3=makeQuery(id+"F18.imprint","IMPRINT",FACE,{"disambiguationData":[TD([[makeQuery(id+"F18.imprint","IMPRINT",EDGE,{"derivedFrom":sQuery(id+"F18.wireOp",EDGE,"E129")}),1.0]])]});
            extrude(context, id + "F19", {"entities" : qUnion([Q0, Q1, Q2, Q3]), "operationType" : NewBodyOperationType.REMOVE, "oppositeDirection" : true, "depth" : -1 * mm, "offsetDistance" : 25 * mm});
        }
        {
            var Q0;
            Q0=makeQuery(id+"F1.opExtrude","CAP_FACE",FACE,{"disambiguationData":[OSD([sQuery(id+"F0.wireOp",EDGE,"E0.bottom"),sQuery(id+"F0.wireOp",EDGE,"E0.left"),sQuery(id+"F0.wireOp",EDGE,"E0.right"),sQuery(id+"F0.wireOp",EDGE,"E1.bottom"),sQuery(id+"F0.wireOp",EDGE,"E2.bottom"),sQuery(id+"F0.wireOp",EDGE,"E4")])],"isStart":true});
            var sketch = newSketch(context, id + "F20", { "sketchPlane" : qUnion([Q0])});
            skLineSegment(sketch, "E132.bottom", {"start": v(-9.5, 35) * mm, "end": v(9.5, 35) * mm});
            skLineSegment(sketch, "E132.top", {"start": v(-9.5, 21) * mm, "end": v(9.5, 21) * mm});
            skLineSegment(sketch, "E132.left", {"start": v(-9.5, 35) * mm, "end": v(-9.5, 21) * mm});
            skLineSegment(sketch, "E132.right", {"start": v(9.5, 35) * mm, "end": v(9.5, 21) * mm});
            skPoint(sketch, "E133", {"position": v(0, 35) * mm});
            skSolve(sketch);
        }
        {
            var Q0;
            Q0 = qSketchRegion(id + "F20", true);
            extrude(context, id + "F21", {"entities" : qUnion([Q0]), "operationType" : NewBodyOperationType.REMOVE, "oppositeDirection" : true, "depth" : 2 * mm, "offsetDistance" : 25 * mm});
        }
        {
            var Q0;
            Q0 = qSketchRegion(id + "F5", true);
            extrude(context, id + "F22", {"entities" : qUnion([Q0]), "operationType" : NewBodyOperationType.ADD, "depth" : 16 * mm, "offsetDistance" : 25 * mm, "hasSecondDirection" : true, "secondDirectionOppositeDirection" : true, "secondDirectionDepth" : 14 * mm});
        }
    });
